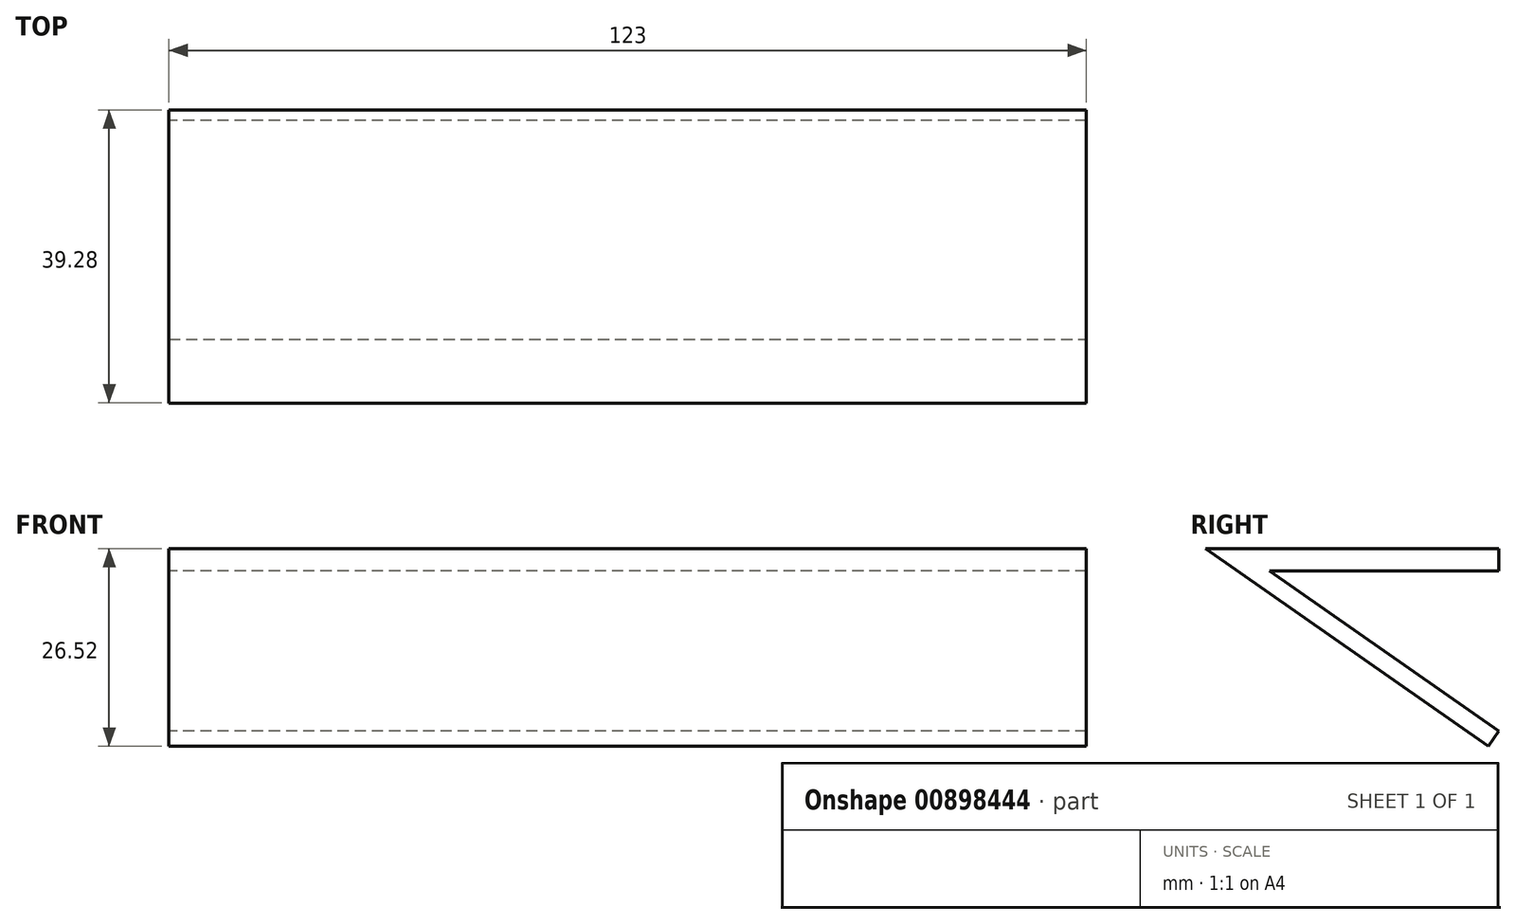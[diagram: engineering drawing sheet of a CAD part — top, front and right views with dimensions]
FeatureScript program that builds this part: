
annotation { "Feature Type Name" : "Feature", "Feature Type Description" : "" }
export const myFeature = defineFeature(function(context is Context, id is Id, definition is map)
    precondition{}
    {
        {
            var Q0;
            Q0=qCreatedBy(makeId("Right.planeOp"),FACE);
            var sketch = newSketch(context, id + "F0", { "sketchPlane" : qUnion([Q0])});
            skLineSegment(sketch, "E0.bottom", {"start": v(0, 0) * mm, "end": v(-35, 0) * mm});
            skLineSegment(sketch, "E0.top", {"start": v(0, 3) * mm, "end": v(-35, 3) * mm});
            skLineSegment(sketch, "E0.left", {"start": v(0, 3) * mm, "end": v(0, 0) * mm});
            skLineSegment(sketch, "E0.right", {"start": v(-35, 3) * mm, "end": v(-35, 0) * mm});
            skSolve(sketch);
        }
        {
            var Q0;
            Q0 = qSketchRegion(id + "F0", true);
            extrude(context, id + "F1", {"entities" : qUnion([Q0]), "depth" : 123 * mm, "offsetDistance" : 25 * mm});
        }
        {
            var Q0;
            Q0=makeQuery(id+"F1.opExtrude","CAP_FACE",FACE,{"disambiguationData":[OSD([sQuery(id+"F0.wireOp",EDGE,"E0.bottom"),sQuery(id+"F0.wireOp",EDGE,"E0.top"),sQuery(id+"F0.wireOp",EDGE,"E0.left"),sQuery(id+"F0.wireOp",EDGE,"E0.right")])],"isStart":true});
            var sketch = newSketch(context, id + "F2", { "sketchPlane" : qUnion([Q0])});
            skLineSegment(sketch, "E1", {"start": v(35, 3) * mm, "end": v(0, -21.5) * mm});
            skLineSegment(sketch, "E2", {"start": v(35, 0) * mm, "end": v(1.4, -23.52) * mm});
            skLineSegment(sketch, "E3", {"start": v(0, -21.5) * mm, "end": v(1.4, -23.52) * mm});
            skLineSegment(sketch, "E4", {"start": v(0, 0) * mm, "end": v(0, -39.54) * mm, "construction": true});
            skLineSegment(sketch, "E5", {"start": v(35, 3) * mm, "end": v(39.28, 3) * mm});
            skLineSegment(sketch, "E6", {"start": v(39.28, 3) * mm, "end": v(35, 0) * mm});
            skSolve(sketch);
        }
        {
            var Q0;
            Q0 = qSketchRegion(id + "F2", true);
            var Q1;
            {var subQ4=sQuery(id+"F2.wireOp",EDGE,"E2");Q1=makeQuery(id+"F2.imprint","IMPRINT",FACE,{"disambiguationData":[TD([[makeQuery(id+"F2.imprint","IMPRINT",EDGE,{"derivedFrom":subQ4}),-1.0]])]});}
            var Q2;
            Q2=makeQuery(id+"F1.opExtrude","CAP_FACE",FACE,{"disambiguationData":[OSD([sQuery(id+"F0.wireOp",EDGE,"E0.bottom"),sQuery(id+"F0.wireOp",EDGE,"E0.top"),sQuery(id+"F0.wireOp",EDGE,"E0.left"),sQuery(id+"F0.wireOp",EDGE,"E0.right")])],"isStart":false});
            var Q3;
            Q3=makeQuery(id+"F1.opExtrude","CAP_VERTEX",VERTEX,{"disambiguationData":[OSD([sQuery(id+"F0.wireOp",EDGE,"E0.bottom"),sQuery(id+"F0.wireOp",EDGE,"E0.right")])],"isStart":false});
            extrude(context, id + "F3", {"entities" : qUnion([Q0, Q1]), "operationType" : NewBodyOperationType.ADD, "endBound" : BoundingType.UP_TO_SURFACE, "oppositeDirection" : true, "depth" : 50 * mm, "endBoundEntityFace" : qUnion([Q2]), "endBoundEntityVertex" : qUnion([Q3]), "offsetDistance" : 25 * mm});
        }
    });
